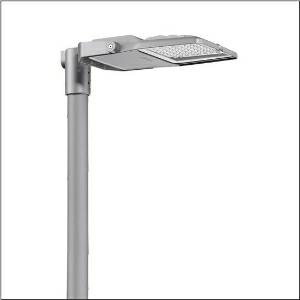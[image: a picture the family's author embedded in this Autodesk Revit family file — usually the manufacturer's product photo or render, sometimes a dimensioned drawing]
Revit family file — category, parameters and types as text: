
# Revit family: floodlight_fl_21_mini___pl61_5xa7776b4c3a_7d7f
name_source: partatom
category: Lighting Fixtures
units: mm (PartAtom-declared; Revit-internal decimal feet)

## family parameters
Cut with Voids When Loaded = No
Host = Face
Light Source = No
Part Type = Normal
Room Calculation Point = No
Round Connector Dimension = Use Diameter
Shared = No

## types (1)
- --- (1 x LED, 6360 lm, 45.7 W, 4000K)
    Apparent Load = 46 VA
    CIE Flux Codes = 33 65 98 100 100
    Color Rendering = 70
    Color Temperature = 4000K
    Default Elevation = 1800 mm
    Description = Floodlight FL 21 mini, floodlight, primary light control with lens, of PMMA, primary optical cover: protective disc, of toughened safety glass, transparent, light distribution: PL61, light emission: direct distribution, installation type: surface-mounted, LED, High Power LED, rated luminous flux: 6.360lm, luminous efficacy: 139lm/W, light colour: 740, colour temperature: 4000K, control gear: D4iSmart Interface (Zhaga), control: overheat protection, constant luminous flux control, time-dependent luminous flux control, flexible luminous flux parameterisation, pre-setting: logarithmic dimming characteristic, with terminal, 6-pole, mains connection: 220..240V, AC, 50/60Hz, start of lifetime: 46W, end of service life: 48W, reduction: 22W, mast bracket, of diecast aluminium, powder-coated, Siteco® metallic grey (DB 702S), corrosivity category C5 mid according to DIN EN ISO 12944, suitable for swimming pools, chlorine-resistant, sealing non-destructively replaceable, mast bracket, of steel, galvanised, powder-coated, Siteco® metallic grey (DB 702S), Smart Interface below and above, protection rating (complete): IP66, insulation class (complete): insulation class II (safety insulation), certification: CE, ENEC, VDE, protection symbol: D, impact resistance: IK08, permissible operating ambient temperature: -40..+40°C, permissible operating ambient temperature for outdoor applications: -40..+50°C, standard: DIN EN 12944, LABS conformity tested according to VDMA 24364:2018-05, packaging unit: 1 piece

Light Distribution: PL61
    Height = 70 mm
    Lamp = 1 x LED
    Lamp Light Flux = 6360 lm
    Lamp Power = 45.7 W
    Lamp count = 1
    Length = 485 mm
    Luminous efficacy = 139 lm/W
    Manufacturer = Siteco
    ModVariant = No
    Model = 5XA7776B4C3A
    Number of Poles = 1
    OnlyDefault = Yes
    Power Factor = 1
    Product Name = Floodlight FL 21 mini | PL61
    Product group = floodlight | pylon annexe
    ProductGroupID = 6201
    Protection Class = Protection class II
    Protection Degree = IP 66
    RLX_Detail_Level = 1
    RLX_Emergency_Light_Flux = 0 lm
    RLX_Emergency_Type = 0
    RLX_Emergency_Type_DB = No
    RlxData = <blob elided: 100969 chars, md5=5df0d200>
    Socket = socket
    Standby Power = 0 W
    System Light Flux = 6360 lm
    System Power = 46 W
    Type Comments = factory setting: luminous flux: 100 % | dim-lin: 254 | 463 mA
    Type Image = l_1007125.jpg
    URL = http://relux.com
    VarID = @adj_122005
    Voltage = 0 V
    Weight = 0.00 kg
    Width = 337 mm

## geometry (parser evidence)
native form markers: Blend x4, Sweep x13
no freeform markers — native parametric forms only
